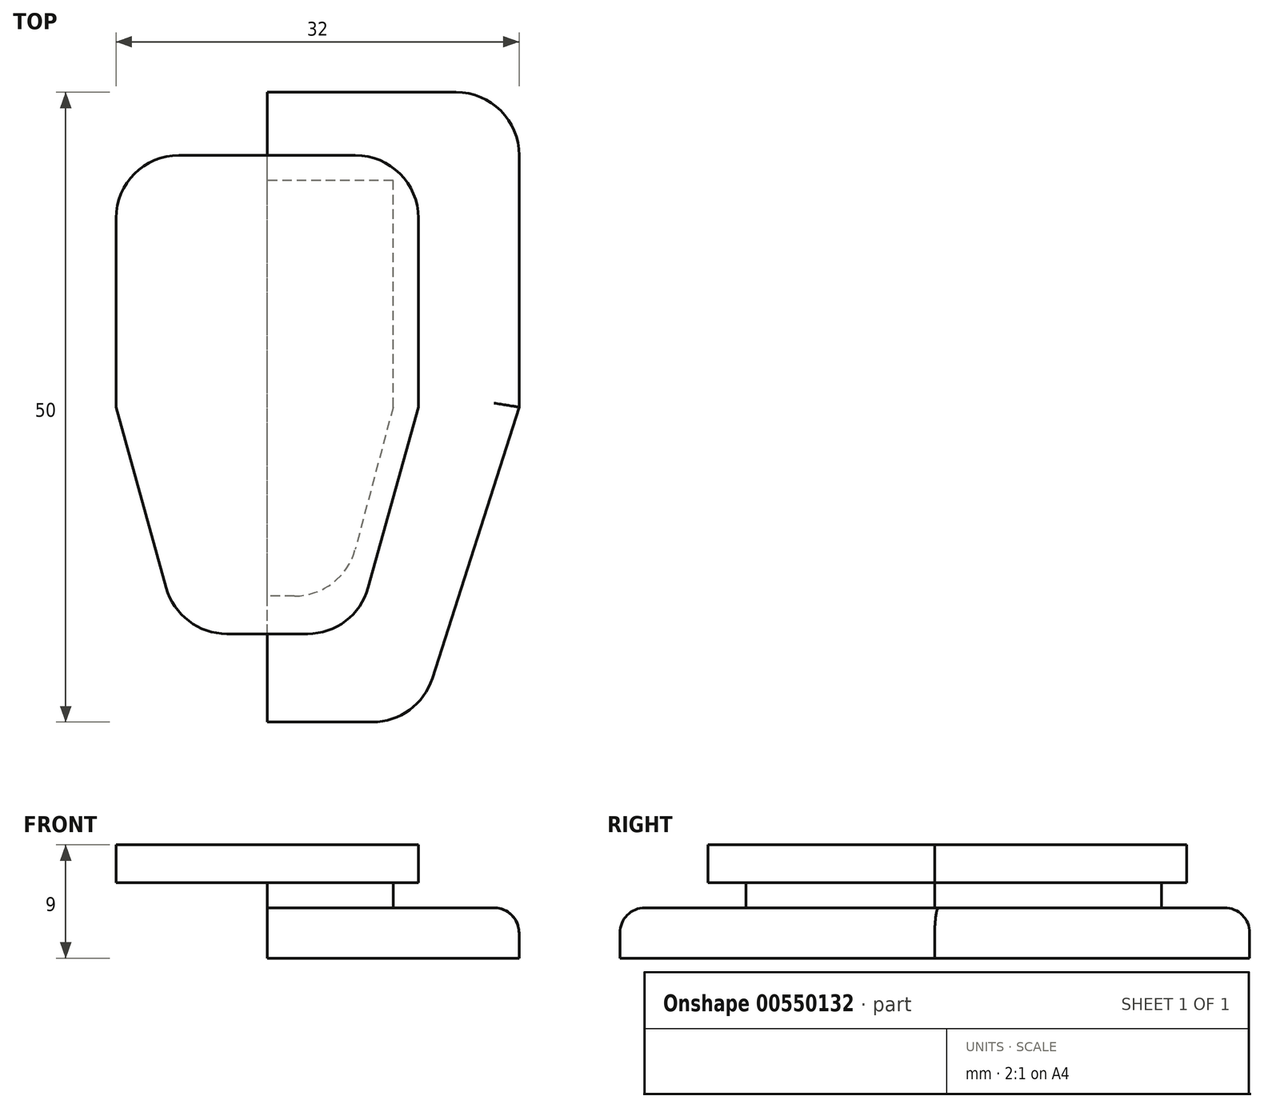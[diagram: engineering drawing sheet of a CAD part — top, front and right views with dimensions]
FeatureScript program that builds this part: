
annotation { "Feature Type Name" : "Feature", "Feature Type Description" : "" }
export const myFeature = defineFeature(function(context is Context, id is Id, definition is map)
    precondition{}
    {
        {
            var Q0;
            Q0=qCreatedBy(makeId("Top.planeOp"),FACE);
            var sketch = newSketch(context, id + "F0", { "sketchPlane" : qUnion([Q0])});
            skLineSegment(sketch, "E0", {"start": v(0, 0) * mm, "end": v(0, 25) * mm});
            skLineSegment(sketch, "E1", {"start": v(0, 25) * mm, "end": v(20, 25) * mm});
            skLineSegment(sketch, "E2", {"start": v(20, 25) * mm, "end": v(20, 0) * mm});
            skLineSegment(sketch, "E3", {"start": v(0, 0) * mm, "end": v(0, -25) * mm});
            skLineSegment(sketch, "E4", {"start": v(0, -25) * mm, "end": v(12, -25) * mm});
            skLineSegment(sketch, "E5", {"start": v(12, -25) * mm, "end": v(20, 0) * mm});
            skSolve(sketch);
        }
        {
            var Q0;
            Q0 = qSketchRegion(id + "F0", true);
            extrude(context, id + "F1", {"entities" : qUnion([Q0]), "depth" : 4 * mm, "offsetDistance" : 25 * mm});
        }
        {
            var Q0;
            Q0=makeQuery(id+"F1.opExtrude","SWEPT_EDGE",EDGE,{"disambiguationData":[OSD([sQuery(id+"F0.wireOp",EDGE,"E4"),sQuery(id+"F0.wireOp",EDGE,"E5")])]});
            var Q1;
            Q1=makeQuery(id+"F1.opExtrude","SWEPT_EDGE",EDGE,{"disambiguationData":[OSD([sQuery(id+"F0.wireOp",EDGE,"E1"),sQuery(id+"F0.wireOp",EDGE,"E2")])]});
            fillet(context, id + "F2", {"entities" : qUnion([Q0, Q1]), "radius" : 5 * mm, "tangentPropagation" : true, "allowEdgeOverflow" : false});
        }
        {
            var Q0;
            Q0=makeQuery(id+"F1.opExtrude","CAP_EDGE",EDGE,{"disambiguationData":[OSD([sQuery(id+"F0.wireOp",EDGE,"E4")])],"isStart":false});
            var Q1;
            Q1=makeQuery(id+"F1.opExtrude","CAP_EDGE",EDGE,{"disambiguationData":[OSD([sQuery(id+"F0.wireOp",EDGE,"E2")])],"isStart":false});
            fillet(context, id + "F3", {"entities" : qUnion([Q0, Q1]), "radius" : 2 * mm, "tangentPropagation" : true, "allowEdgeOverflow" : false});
        }
        {
            var Q0;
            Q0=qCreatedBy(makeId("Top.planeOp"),FACE);
            var sketch = newSketch(context, id + "F4", { "sketchPlane" : qUnion([Q0])});
            skLineSegment(sketch, "E6", {"start": v(0, 0) * mm, "end": v(0, 18) * mm});
            skLineSegment(sketch, "E7", {"start": v(0, 18) * mm, "end": v(10, 18) * mm});
            skLineSegment(sketch, "E8", {"start": v(10, 18) * mm, "end": v(10, 0) * mm});
            skLineSegment(sketch, "E9", {"start": v(0, 0) * mm, "end": v(0, -15) * mm});
            skLineSegment(sketch, "E10", {"start": v(0, -15) * mm, "end": v(6, -15) * mm});
            skLineSegment(sketch, "E11", {"start": v(6, -15) * mm, "end": v(10, 0) * mm});
            skSolve(sketch);
        }
        {
            var Q0;
            Q0 = qSketchRegion(id + "F4", true);
            extrude(context, id + "F5", {"entities" : qUnion([Q0]), "operationType" : NewBodyOperationType.ADD, "depth" : 6 * mm, "offsetDistance" : 25 * mm});
        }
        {
            var Q0;
            Q0=makeQuery(id+"F5.opExtrude","SWEPT_EDGE",EDGE,{"disambiguationData":[OSD([sQuery(id+"F4.wireOp",EDGE,"E10"),sQuery(id+"F4.wireOp",EDGE,"E11")])]});
            fillet(context, id + "F6", {"entities" : qUnion([Q0]), "radius" : 5 * mm, "tangentPropagation" : true, "allowEdgeOverflow" : false});
        }
        {
            var Q0;
            Q0=qCreatedBy(makeId("Top.planeOp"),FACE);
            var sketch = newSketch(context, id + "F7", { "sketchPlane" : qUnion([Q0])});
            skLineSegment(sketch, "E12", {"start": v(0, 0) * mm, "end": v(0, 20) * mm});
            skLineSegment(sketch, "E13", {"start": v(0, 20) * mm, "end": v(12, 20) * mm});
            skLineSegment(sketch, "E14", {"start": v(12, 20) * mm, "end": v(12, 0) * mm});
            skLineSegment(sketch, "E15", {"start": v(0, 0) * mm, "end": v(0, -18) * mm});
            skLineSegment(sketch, "E16", {"start": v(0, -18) * mm, "end": v(7, -18) * mm});
            skLineSegment(sketch, "E17", {"start": v(7, -18) * mm, "end": v(12, 0) * mm});
            skSolve(sketch);
        }
        {
            var Q0;
            Q0 = qSketchRegion(id + "F7", true);
            extrude(context, id + "F8", {"entities" : qUnion([Q0]), "depth" : 3 * mm, "offsetDistance" : 25 * mm});
        }
        {
            var Q0;
            Q0=makeQuery(id+"F8.opExtrude","SWEPT_BODY",BODY,{"disambiguationData":[OSD([sQuery(id+"F7.wireOp",EDGE,"E12"),sQuery(id+"F7.wireOp",EDGE,"E13"),sQuery(id+"F7.wireOp",EDGE,"E14"),sQuery(id+"F7.wireOp",EDGE,"E15"),sQuery(id+"F7.wireOp",EDGE,"E16"),sQuery(id+"F7.wireOp",EDGE,"E17")])]});
            transform(context, id + "F9", {"entities" : qUnion([Q0]), "transformType" : TransformType.TRANSLATION_3D, "dx" : 0 * mm, "dy" : 0 * mm, "dz" : 6 * mm, "makeCopy" : false});
        }
        {
            var Q0;
            Q0=makeQuery(id+"F8.opExtrude","SWEPT_EDGE",EDGE,{"disambiguationData":[OSD([sQuery(id+"F7.wireOp",EDGE,"E16"),sQuery(id+"F7.wireOp",EDGE,"E17")])]});
            var Q1;
            Q1=makeQuery(id+"F8.opExtrude","SWEPT_EDGE",EDGE,{"disambiguationData":[OSD([sQuery(id+"F7.wireOp",EDGE,"E13"),sQuery(id+"F7.wireOp",EDGE,"E14")])]});
            fillet(context, id + "F10", {"entities" : qUnion([Q0, Q1]), "radius" : 5 * mm, "tangentPropagation" : true, "allowEdgeOverflow" : false});
        }
        {
            var Q0;
            Q0=makeQuery(id+"F8.opExtrude","SWEPT_BODY",BODY,{"disambiguationData":[OSD([sQuery(id+"F7.wireOp",EDGE,"E12"),sQuery(id+"F7.wireOp",EDGE,"E13"),sQuery(id+"F7.wireOp",EDGE,"E14"),sQuery(id+"F7.wireOp",EDGE,"E15"),sQuery(id+"F7.wireOp",EDGE,"E16"),sQuery(id+"F7.wireOp",EDGE,"E17")])]});
            var Q1;
            Q1=qCreatedBy(makeId("Right.planeOp"),FACE);
            mirror(context, id + "F11", {"operationType" : NewBodyOperationType.ADD, "entities" : qUnion([Q0]), "mirrorPlane" : qUnion([Q1])});
        }
    });
